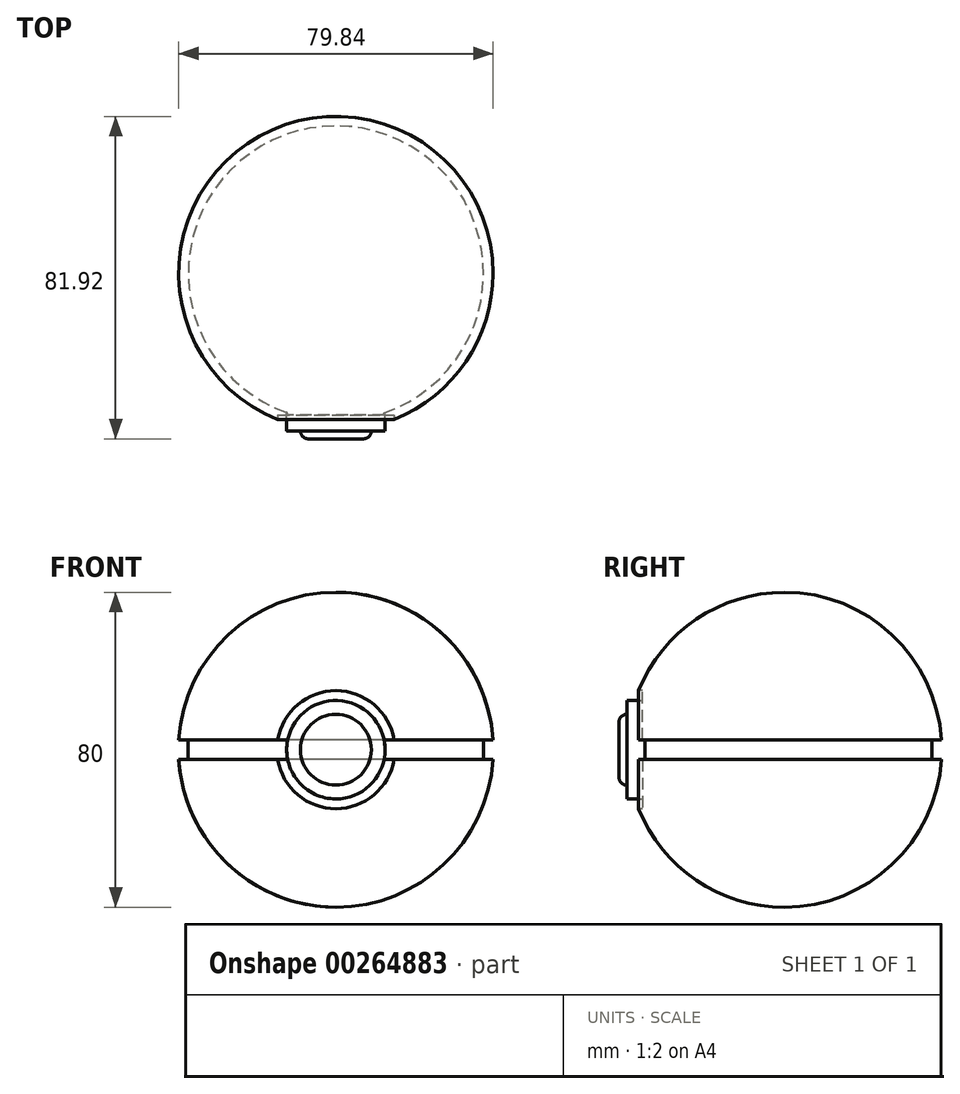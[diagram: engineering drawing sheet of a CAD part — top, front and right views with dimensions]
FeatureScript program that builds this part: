
annotation { "Feature Type Name" : "Feature", "Feature Type Description" : "" }
export const myFeature = defineFeature(function(context is Context, id is Id, definition is map)
    precondition{}
    {
        {
            var Q0;
            Q0=qCreatedBy(makeId("Front.planeOp"),FACE);
            var sketch = newSketch(context, id + "F0", { "sketchPlane" : qUnion([Q0])});
            skArc(sketch, "E0", {"start": v(0, -40) * mm, "mid": v(27.39, -29.15) * mm, "end": v(39.92, -2.5) * mm});
            skLineSegment(sketch, "E1", {"start": v(0, 40) * mm, "end": v(0, -40) * mm});
            skLineSegment(sketch, "E2", {"start": v(40, 0) * mm, "end": v(37.5, 0) * mm, "construction": true});
            skPoint(sketch, "E2.endSnap0", {"position": v(40, 0) * mm});
            skLineSegment(sketch, "E3", {"start": v(37.5, 0) * mm, "end": v(37.5, 2.5) * mm});
            skLineSegment(sketch, "E4", {"start": v(37.5, 2.5) * mm, "end": v(39.92, 2.5) * mm});
            skLineSegment(sketch, "E5.MirrorCS", {"start": v(37.5, 0) * mm, "end": v(37.5, -2.5) * mm});
            skLineSegment(sketch, "E6.MirrorCS", {"start": v(37.5, -2.5) * mm, "end": v(39.92, -2.5) * mm});
            skArc(sketch, "E7.trimOffspring", {"start": v(39.92, 2.5) * mm, "mid": v(27.39, 29.15) * mm, "end": v(0, 40) * mm});
            skSolve(sketch);
        }
        {
            var Q0;
            Q0=makeQuery(id+"F0.imprint","IMPRINT",FACE,{"disambiguationData":[TD([[makeQuery(id+"F0.imprint","IMPRINT",EDGE,{"derivedFrom":sQuery(id+"F0.wireOp",EDGE,"E0")}),1.0]])]});
            var Q1;
            Q1=sQuery(id+"F0.wireOp",EDGE,"E1");
            revolve(context, id + "F1", {"entities" : qUnion([Q0]), "axis" : qUnion([Q1]), "revolveType" : RevolveType.FULL});
        }
        {
            var Q0;
            Q0=qCreatedBy(makeId("Front.planeOp"),FACE);
            var sketch = newSketch(context, id + "F2", { "sketchPlane" : qUnion([Q0])});
            skCircle(sketch, "E8", {"center": v(0, 0) * mm, "radius": 12.5 * mm});
            skSolve(sketch);
        }
        {
            var Q0;
            Q0 = qSketchRegion(id + "F2", true);
            extrude(context, id + "F3", {"entities" : qUnion([Q0]), "operationType" : NewBodyOperationType.ADD, "depth" : 40 * mm});
        }
        {
            var Q0;
            Q0=makeQuery(id+"F3.opExtrude","CAP_FACE",FACE,{"disambiguationData":[OSD([sQuery(id+"F2.wireOp",EDGE,"E8")])],"isStart":false});
            var sketch = newSketch(context, id + "F4", { "sketchPlane" : qUnion([Q0])});
            skCircle(sketch, "E9", {"center": v(0, 0) * mm, "radius": 12.5 * mm});
            skCircle(sketch, "E10", {"center": v(0, 0) * mm, "radius": 15 * mm});
            skSolve(sketch);
        }
        {
            var Q0;
            Q0 = qSketchRegion(id + "F4", true);
            extrude(context, id + "F5", {"entities" : qUnion([Q0]), "operationType" : NewBodyOperationType.REMOVE, "oppositeDirection" : true, "depth" : 4 * mm});
        }
        {
            var Q0;
            Q0=makeQuery(id+"F3.opExtrude","CAP_FACE",FACE,{"disambiguationData":[OSD([sQuery(id+"F2.wireOp",EDGE,"E8")])],"isStart":false});
            var sketch = newSketch(context, id + "F6", { "sketchPlane" : qUnion([Q0])});
            skCircle(sketch, "E11", {"center": v(0, 0) * mm, "radius": 9 * mm});
            skSolve(sketch);
        }
        {
            var Q0;
            Q0 = qSketchRegion(id + "F6", true);
            extrude(context, id + "F7", {"entities" : qUnion([Q0]), "operationType" : NewBodyOperationType.ADD, "depth" : 2 * mm});
        }
        {
            var Q0;
            Q0=makeQuery(id+"F7.opExtrude","CAP_EDGE",EDGE,{"disambiguationData":[OSD([sQuery(id+"F6.wireOp",EDGE,"E11")])],"isStart":false});
            fillet(context, id + "F8", {"entities" : qUnion([Q0]), "radius" : 2 * mm, "tangentPropagation" : true, "allowEdgeOverflow" : false});
        }
    });
